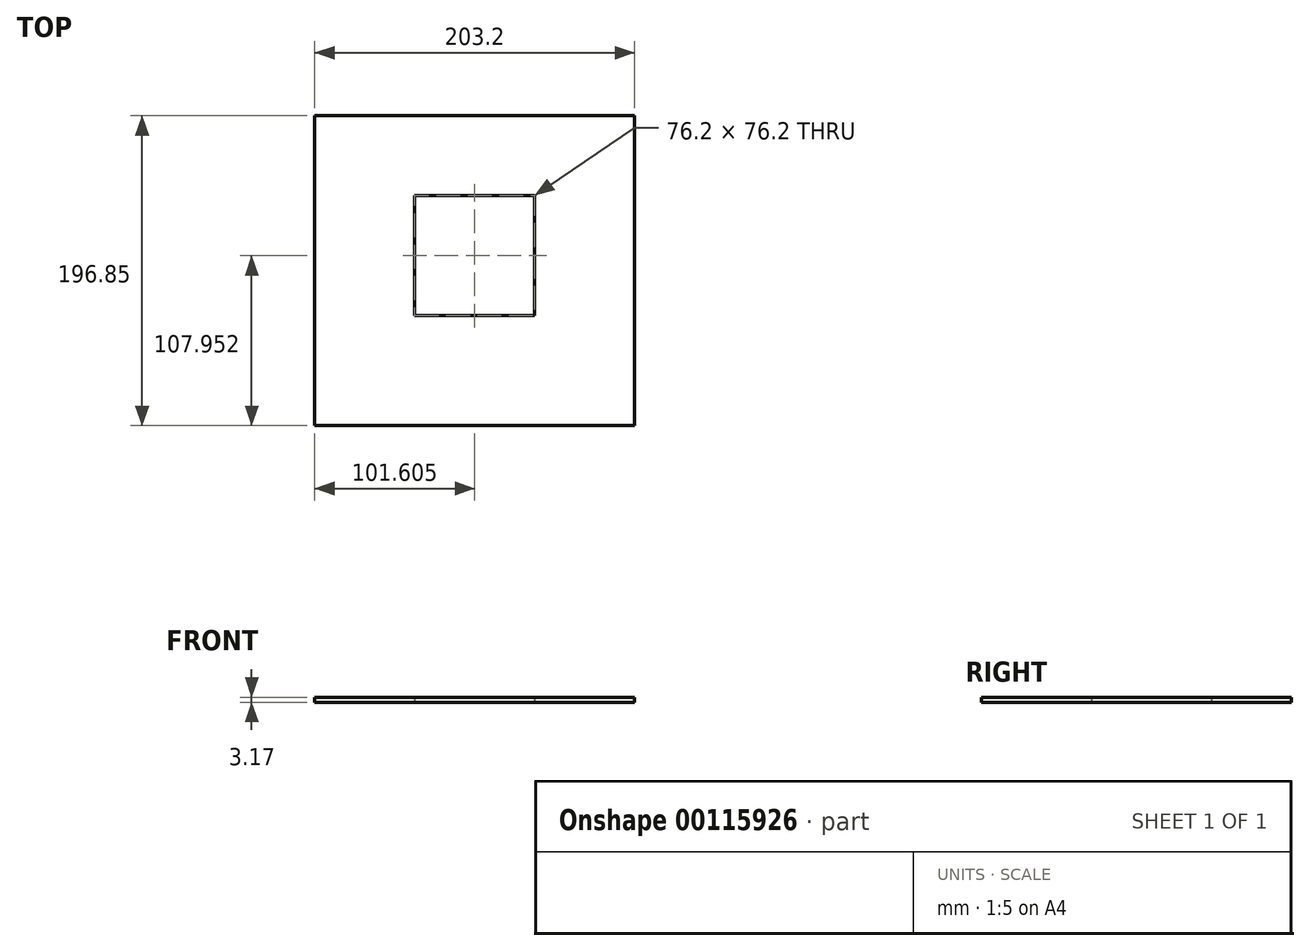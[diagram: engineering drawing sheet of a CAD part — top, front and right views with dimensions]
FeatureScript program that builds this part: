
annotation { "Feature Type Name" : "Feature", "Feature Type Description" : "" }
export const myFeature = defineFeature(function(context is Context, id is Id, definition is map)
    precondition{}
    {
        {
            var Q0;
            Q0=qCreatedBy(makeId("Top.planeOp"),FACE);
            var sketch = newSketch(context, id + "F0", { "sketchPlane" : qUnion([Q0])});
            skLineSegment(sketch, "E0.bottom", {"start": v(-78.85, 111.02) * mm, "end": v(124.35, 111.02) * mm});
            skLineSegment(sketch, "E0.top", {"start": v(-78.85, -85.83) * mm, "end": v(124.35, -85.83) * mm});
            skLineSegment(sketch, "E0.left", {"start": v(-78.85, 111.02) * mm, "end": v(-78.85, -85.83) * mm});
            skLineSegment(sketch, "E0.right", {"start": v(124.35, 111.02) * mm, "end": v(124.35, -85.83) * mm});
            skLineSegment(sketch, "E1.bottom", {"start": v(-15.35, 60.22) * mm, "end": v(60.85, 60.22) * mm});
            skLineSegment(sketch, "E1.top", {"start": v(-15.35, -15.98) * mm, "end": v(60.85, -15.98) * mm});
            skLineSegment(sketch, "E1.left", {"start": v(-15.35, 60.22) * mm, "end": v(-15.35, -15.98) * mm});
            skLineSegment(sketch, "E1.right", {"start": v(60.85, 60.22) * mm, "end": v(60.85, -15.98) * mm});
            skSolve(sketch);
        }
        {
            var Q0;
            Q0=makeQuery(id+"F0.imprint","IMPRINT",FACE,{"disambiguationData":[TD([[makeQuery(id+"F0.imprint","IMPRINT",EDGE,{"derivedFrom":sQuery(id+"F0.wireOp",EDGE,"E0.bottom")}),-1.0]])]});
            extrude(context, id + "F1", {"entities" : qUnion([Q0]), "depth" : 3.17 * mm});
        }
    });
